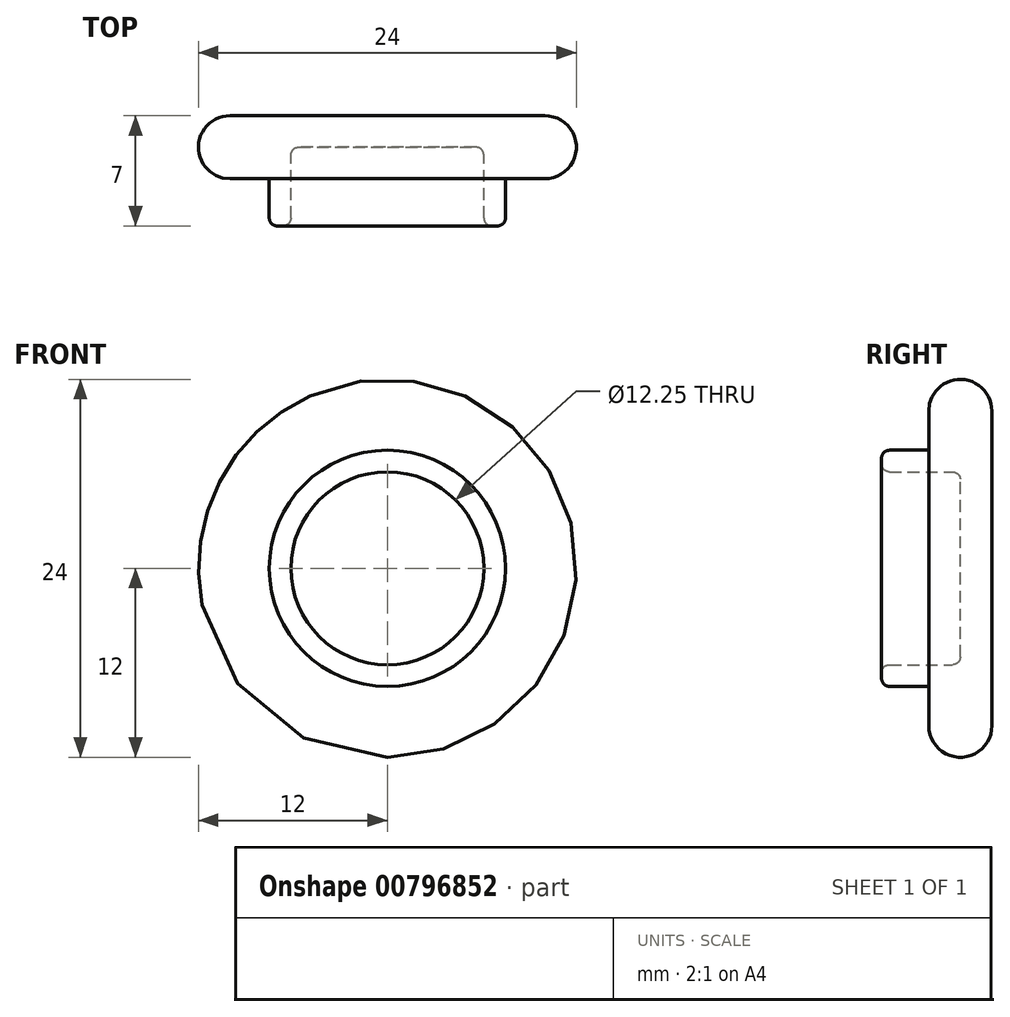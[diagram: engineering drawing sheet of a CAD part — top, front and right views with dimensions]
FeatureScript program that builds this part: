
annotation { "Feature Type Name" : "Feature", "Feature Type Description" : "" }
export const myFeature = defineFeature(function(context is Context, id is Id, definition is map)
    precondition{}
    {
        {
            var Q0;
            Q0=qCreatedBy(makeId("Front.planeOp"),FACE);
            var sketch = newSketch(context, id + "F0", { "sketchPlane" : qUnion([Q0])});
            skCircle(sketch, "E0", {"center": v(0, 0) * mm, "radius": 6.12 * mm});
            skCircle(sketch, "E1", {"center": v(0, 0) * mm, "radius": 7.5 * mm});
            skCircle(sketch, "E2", {"center": v(0, 0) * mm, "radius": 12 * mm});
            skSolve(sketch);
        }
        {
            var Q0;
            Q0=makeQuery(id+"F0.imprint","IMPRINT",FACE,{"disambiguationData":[TD([[makeQuery(id+"F0.imprint","IMPRINT",EDGE,{"derivedFrom":sQuery(id+"F0.wireOp",EDGE,"E1")}),-1.0]])]});
            var Q1;
            Q1=makeQuery(id+"F0.imprint","IMPRINT",FACE,{"disambiguationData":[TD([[makeQuery(id+"F0.imprint","IMPRINT",EDGE,{"derivedFrom":sQuery(id+"F0.wireOp",EDGE,"E0")}),-1.0]])]});
            var Q2;
            Q2=makeQuery(id+"F0.imprint","IMPRINT",FACE,{"disambiguationData":[TD([[makeQuery(id+"F0.imprint","IMPRINT",EDGE,{"derivedFrom":sQuery(id+"F0.wireOp",EDGE,"E0")}),1.0]])]});
            extrude(context, id + "F1", {"entities" : qUnion([Q0, Q1, Q2]), "oppositeDirection" : true, "depth" : 4 * mm, "offsetDistance" : 25 * mm});
        }
        {
            var Q0;
            Q0=makeQuery(id+"F0.imprint","IMPRINT",FACE,{"disambiguationData":[TD([[makeQuery(id+"F0.imprint","IMPRINT",EDGE,{"derivedFrom":sQuery(id+"F0.wireOp",EDGE,"E0")}),-1.0]])]});
            var Q1;
            Q1=sQuery(id+"F0.wireOp",EDGE,"E0");
            var Q2;
            Q2=sQuery(id+"F0.wireOp",EDGE,"E1");
            extrude(context, id + "F2", {"entities" : qUnion([Q0]), "operationType" : NewBodyOperationType.ADD, "surfaceEntities" : qUnion([Q1, Q2]), "depth" : 3 * mm, "offsetDistance" : 25 * mm});
        }
        {
            var Q0;
            Q0=makeQuery(id+"F0.imprint","IMPRINT",FACE,{"disambiguationData":[TD([[makeQuery(id+"F0.imprint","IMPRINT",EDGE,{"derivedFrom":sQuery(id+"F0.wireOp",EDGE,"E0")}),1.0]])]});
            extrude(context, id + "F3", {"entities" : qUnion([Q0]), "operationType" : NewBodyOperationType.REMOVE, "oppositeDirection" : true, "depth" : 2 * mm, "offsetDistance" : 25 * mm});
        }
        {
            var Q0;
            Q0=makeQuery(id+"F2.opExtrude","CAP_EDGE",EDGE,{"disambiguationData":[OSD([sQuery(id+"F0.wireOp",EDGE,"E1")])],"isStart":true});
            var Q1;
            Q1=makeQuery(id+"F1.opExtrude","CAP_EDGE",EDGE,{"disambiguationData":[OSD([sQuery(id+"F0.wireOp",EDGE,"E2")])],"isStart":true});
            var Q2;
            Q2=makeQuery(id+"F1.opExtrude","CAP_EDGE",EDGE,{"disambiguationData":[OSD([sQuery(id+"F0.wireOp",EDGE,"E2")])],"isStart":false});
            fillet(context, id + "F4", {"entities" : qUnion([Q0, Q1, Q2]), "radius" : 2 * mm, "tangentPropagation" : true, "allowEdgeOverflow" : false});
        }
        {
            var Q0;
            Q0=makeQuery(id+"F2.opExtrude","CAP_EDGE",EDGE,{"disambiguationData":[OSD([sQuery(id+"F0.wireOp",EDGE,"E1")])],"isStart":false});
            var Q1;
            Q1=makeQuery(id+"F2.opExtrude","CAP_EDGE",EDGE,{"disambiguationData":[OSD([sQuery(id+"F0.wireOp",EDGE,"E0")])],"isStart":false});
            var Q2;
            Q2=makeQuery(id+"F3.boolean.opBoolean","COPY",EDGE,{"derivedFrom":makeQuery(id+"F3.opExtrude","CAP_EDGE",EDGE,{"disambiguationData":[OSD([sQuery(id+"F0.wireOp",EDGE,"E0")])],"isStart":false})});
            fillet(context, id + "F5", {"entities" : qUnion([Q0, Q1, Q2]), "radius" : .5 * mm, "tangentPropagation" : true, "allowEdgeOverflow" : false});
        }
    });
